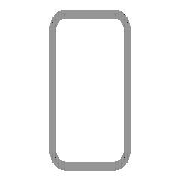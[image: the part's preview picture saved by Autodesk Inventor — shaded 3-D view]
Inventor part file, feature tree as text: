
AUTODESK INVENTOR PART (.ipt)
format: ipt  version: 2025 (Build 290162010, 162A)  size: 143,872 bytes
history: native  units: mm (DEFAULTED — no unit token found)
features: other x4, plane x2, split x1, sketch x1
ambient origin geometry x8: Origin, YZ Plane, XZ Plane, XY Plane, X Axis, Y Axis, Z Axis, Center Point
bodies: Solid1 (feature_tree), Body (feature_tree)
feature tree (8):
  parser-record x1  (decoder bookkeeping rows leaked as tree rows — omitted from the tree; the rows remain in map.json)
  other  "Driven Length"
  other  "Start Plane"
  other  "End Plane"
  plane  "Work Plane5"
  split  "Split2"
  sketch  "Sketch3"  dims[d3=173.0mm d4=0.0mm d7=4.0mm d9=20.0mm d11=40.0mm d12=2.0mm d13=40.0mm d14=213.0mm d15=10.0mm d16=20.0mm d17=90.0deg d18=173.0mm]
  plane  "Work Plane3"
